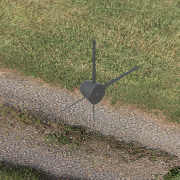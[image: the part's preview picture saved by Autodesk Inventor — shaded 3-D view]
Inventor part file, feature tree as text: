
AUTODESK INVENTOR PART (.ipt)
format: ipt  version: 2021 (Build 250183000, 183)  size: 367,104 bytes
history: native  units: mm
features: sketch x7, thread x6, extrude x2, pattern_circular x2, revolve x1, plane x1, loft x1, hole x1
ambient origin geometry x8: Origin, YZ Plane, XZ Plane, XY Plane, X Axis, Y Axis, Z Axis, Center Point
bodies: Body1 (feature_tree)
feature tree (21):
  revolve  "Revolution2"  [1 undecoded]
  plane  "Work Plane1"
  sketch  "Sketch2"  dims[d7=230.0mm d8=300.0mm]
  sketch  "3D Sketch1"
  sketch  "Sketch3"  dims[d9=280.0mm d10=250.0mm]
  extrude  "Extrusion1"  Depth=300.0mm
  loft  "Loft4"
  pattern_circular  "Circular Pattern1"  Count=100  [1 undecoded]
  hole  "Hole1"  [1 undecoded]
  extrude  "Extrusion2"  TaperAngle=150.0deg  [1 undecoded]
  pattern_circular  "Circular Pattern2"  [2 undecoded]
  thread  "Thread2"  [1 undecoded]
  thread  "Thread3"  [1 undecoded]
  thread  "Thread4"  [1 undecoded]
  thread  "Thread5"  [1 undecoded]
  thread  "Thread6"  [1 undecoded]
  thread  "Thread7"  [1 undecoded]
  sketch  "Sketch1"  dims[d0=175.0mm d1=300.0mm]
  sketch  "Sketch4"  dims[d11=90.0deg d12=1000.0mm]
  sketch  "Sketch5"  dims[d25=45.0mm d26=400.0mm]
  sketch  "Sketch6"  dims[d76=32.0mm d77=0.0mm d81=150.0deg d83=10.0mm d84=4.0mm d85=120.0deg d87=30.0mm d88=8.0mm d89=0.0mm d90=90.0deg d91=0.0mm d92=90.0deg d93=40.0mm d94=360.0deg d96=50.0mm d97=6.0mm d98=4.0mm d99=2.0mm d100=90.0deg d101=50.0mm d102=0.0mm d105=290.0mm d106=20.0mm d107=50.0mm d108=0.0mm d109=60.0mm d110=360.0deg d112=50.0mm d113=0.0mm d114=50.0mm d115=0.0mm d116=50.0mm d117=0.0mm d118=50.0mm d119=0.0mm d120=50.0mm d121=0.0mm d122=50.0mm d123=0.0mm]
note: 12 required parameter values undecoded (feature->parameter linkage not recoverable at this tier; creation-order binding heuristic only, values carry confidence <= 0.55)